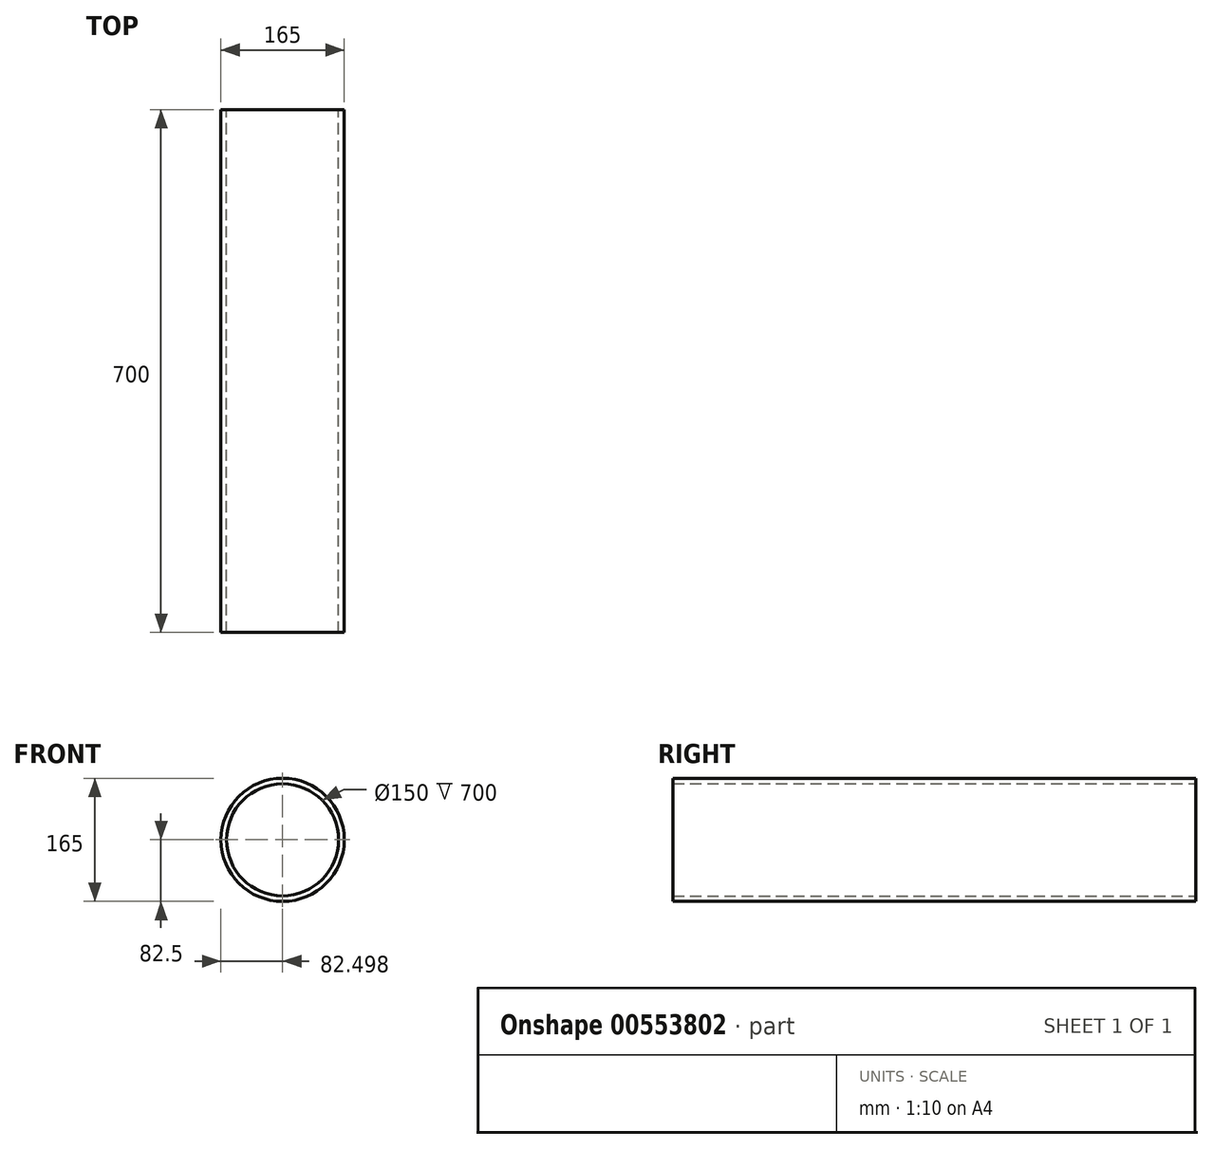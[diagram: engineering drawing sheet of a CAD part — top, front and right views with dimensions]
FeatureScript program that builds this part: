
annotation { "Feature Type Name" : "Feature", "Feature Type Description" : "" }
export const myFeature = defineFeature(function(context is Context, id is Id, definition is map)
    precondition{}
    {
        {
            var Q0;
            Q0=qCreatedBy(makeId("Front.planeOp"),FACE);
            var sketch = newSketch(context, id + "F0", { "sketchPlane" : qUnion([Q0])});
            skCircle(sketch, "E0", {"center": v(3.03, 0) * mm, "radius": 82.5 * mm});
            skCircle(sketch, "E1", {"center": v(3.03, 0) * mm, "radius": 75 * mm});
            skSolve(sketch);
        }
        {
            var Q0;
            Q0=makeQuery(id+"F0.imprint","IMPRINT",FACE,{"disambiguationData":[TD([[makeQuery(id+"F0.imprint","IMPRINT",EDGE,{"derivedFrom":sQuery(id+"F0.wireOp",EDGE,"E0")}),1.0]])]});
            extrude(context, id + "F1", {"entities" : qUnion([Q0]), "endBound" : BoundingType.SYMMETRIC, "depth" : 700 * mm, "offsetDistance" : 25 * mm});
        }
    });
